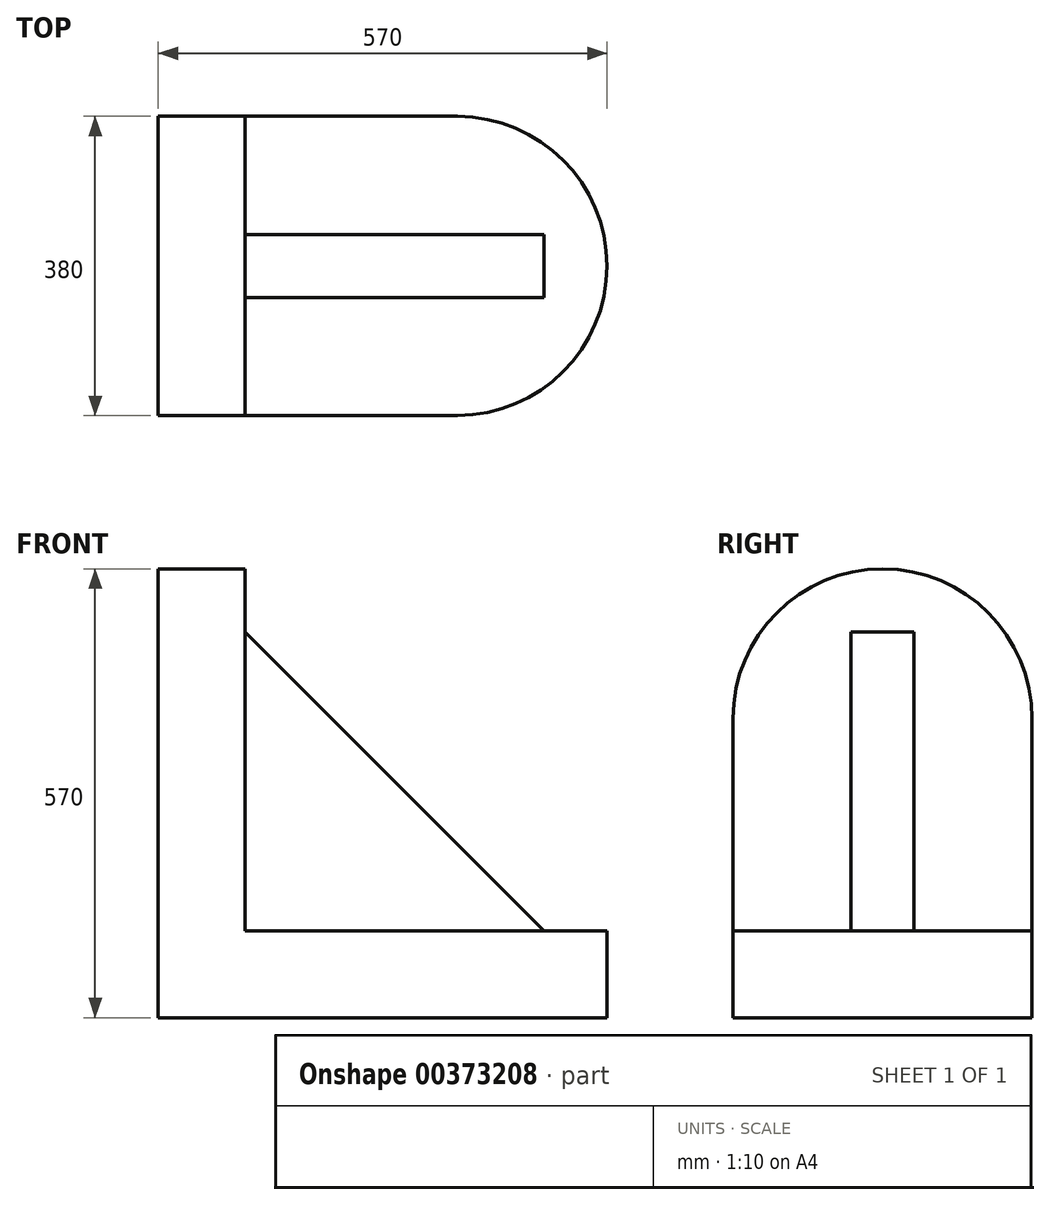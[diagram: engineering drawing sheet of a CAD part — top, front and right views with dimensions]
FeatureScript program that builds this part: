
annotation { "Feature Type Name" : "Feature", "Feature Type Description" : "" }
export const myFeature = defineFeature(function(context is Context, id is Id, definition is map)
    precondition{}
    {
        {
            var Q0;
            Q0=qCreatedBy(makeId("Top.planeOp"),FACE);
            var sketch = newSketch(context, id + "F0", { "sketchPlane" : qUnion([Q0])});
            skLineSegment(sketch, "E0.bottom", {"start": v(0, 0) * mm, "end": v(380, 0) * mm});
            skLineSegment(sketch, "E0.top", {"start": v(0, -380) * mm, "end": v(380, -380) * mm});
            skLineSegment(sketch, "E0.left", {"start": v(0, 0) * mm, "end": v(0, -380) * mm});
            skLineSegment(sketch, "E0.right", {"start": v(380, 0) * mm, "end": v(380, -380) * mm});
            skLineSegment(sketch, "E1", {"start": v(0, -380) * mm, "end": v(110, -380) * mm});
            skCircle(sketch, "E2", {"center": v(380, -190) * mm, "radius": 190 * mm});
            skSolve(sketch);
        }
        {
            var Q0;
            {var subQ1=sQuery(id+"F0.wireOp",EDGE,"E0.bottom");Q0=makeQuery(id+"F0.imprint","IMPRINT",FACE,{"disambiguationData":[TD([[makeQuery(id+"F0.imprint","IMPRINT",EDGE,{"derivedFrom":subQ1}),-1.0]])]});}
            var Q1;
            {var subQ0=sQuery(id+"F0.wireOp",EDGE,"E0.right");Q1=makeQuery(id+"F0.imprint","IMPRINT",FACE,{"disambiguationData":[TD([[makeQuery(id+"F0.imprint","IMPRINT",EDGE,{"derivedFrom":subQ0}),-1.0]])]});}
            var Q2;
            {var subQ0=sQuery(id+"F0.wireOp",EDGE,"E0.right");Q2=makeQuery(id+"F0.imprint","IMPRINT",FACE,{"disambiguationData":[TD([[makeQuery(id+"F0.imprint","IMPRINT",EDGE,{"derivedFrom":subQ0}),1.0]])]});}
            extrude(context, id + "F1", {"entities" : qUnion([Q0, Q1, Q2]), "depth" : 110 * mm});
        }
        {
            var Q0;
            Q0=makeQuery(id+"F1.opExtrude","CAP_FACE",FACE,{"disambiguationData":[OSD([sQuery(id+"F0.wireOp",EDGE,"E0.bottom"),sQuery(id+"F0.wireOp",EDGE,"E0.top"),sQuery(id+"F0.wireOp",EDGE,"E0.left"),sQuery(id+"F0.wireOp",EDGE,"E1"),sQuery(id+"F0.wireOp",EDGE,"E2")])],"isStart":false});
            var sketch = newSketch(context, id + "F2", { "sketchPlane" : qUnion([Q0])});
            skLineSegment(sketch, "E3.bottom", {"start": v(0, 0) * mm, "end": v(110, 0) * mm});
            skLineSegment(sketch, "E3.top", {"start": v(0, -380) * mm, "end": v(110, -380) * mm});
            skLineSegment(sketch, "E3.left", {"start": v(0, 0) * mm, "end": v(0, -380) * mm});
            skLineSegment(sketch, "E3.right", {"start": v(110, 0) * mm, "end": v(110, -380) * mm});
            skSolve(sketch);
        }
        {
            var Q0;
            Q0=makeQuery(id+"F2.imprint","IMPRINT",FACE,{"disambiguationData":[TD([[makeQuery(id+"F2.imprint","IMPRINT",EDGE,{"derivedFrom":sQuery(id+"F2.wireOp",EDGE,"E3.bottom")}),-1.0]])]});
            extrude(context, id + "F3", {"entities" : qUnion([Q0]), "operationType" : NewBodyOperationType.ADD, "depth" : 270 * mm});
        }
        {
            var Q0;
            Q0=makeQuery(id+"F3.boolean.opBoolean","MERGE",FACE,{"derivedFrom":[makeQuery(id+"F1.opExtrude","SWEPT_FACE",FACE,{"disambiguationData":[OSD([sQuery(id+"F0.wireOp",EDGE,"E0.left")])]}),makeQuery(id+"F3.opExtrude","SWEPT_FACE",FACE,{"disambiguationData":[OSD([sQuery(id+"F2.wireOp",EDGE,"E3.left")])]})]});
            var sketch = newSketch(context, id + "F4", { "sketchPlane" : qUnion([Q0])});
            skCircle(sketch, "E4", {"center": v(190, 380) * mm, "radius": 190 * mm});
            skSolve(sketch);
        }
        {
            var Q0;
            {var subQ1=sQuery(id+"F2.wireOp",EDGE,"E3.left");var subQ3=makeQuery(id+"F3.opExtrude","CAP_EDGE",EDGE,{"disambiguationData":[OSD([subQ1])],"isStart":false});Q0=makeQuery(id+"F4.imprint","IMPRINT",FACE,{"disambiguationData":[TD([[makeQuery(id+"F4.imprint","IMPRINT",EDGE,{"derivedFrom":subQ3}),1.0]])]});}
            extrude(context, id + "F5", {"entities" : qUnion([Q0]), "operationType" : NewBodyOperationType.ADD, "oppositeDirection" : true, "depth" : 110 * mm});
        }
        {
            var Q0;
            Q0=makeQuery(id+"F1.opExtrude","CAP_FACE",FACE,{"disambiguationData":[OSD([sQuery(id+"F0.wireOp",EDGE,"E0.bottom"),sQuery(id+"F0.wireOp",EDGE,"E0.top"),sQuery(id+"F0.wireOp",EDGE,"E0.left"),sQuery(id+"F0.wireOp",EDGE,"E1"),sQuery(id+"F0.wireOp",EDGE,"E2")])],"isStart":false});
            var sketch = newSketch(context, id + "F6", { "sketchPlane" : qUnion([Q0])});
            skLineSegment(sketch, "E5", {"start": v(110, -190) * mm, "end": v(490, -190) * mm});
            skLineSegment(sketch, "E6", {"start": v(490, -190) * mm, "end": v(490, -150) * mm});
            skLineSegment(sketch, "E7", {"start": v(490, -150) * mm, "end": v(110, -150) * mm});
            skLineSegment(sketch, "E8", {"start": v(110, -150) * mm, "end": v(110, -230) * mm});
            skLineSegment(sketch, "E9", {"start": v(490, -190) * mm, "end": v(490, -230) * mm});
            skLineSegment(sketch, "E10", {"start": v(490, -230) * mm, "end": v(110, -230) * mm});
            skSolve(sketch);
        }
        {
            var Q0;
            {var subQ0=sQuery(id+"F6.wireOp",EDGE,"E5");Q0=makeQuery(id+"F6.imprint","IMPRINT",FACE,{"disambiguationData":[TD([[makeQuery(id+"F6.imprint","IMPRINT",EDGE,{"derivedFrom":subQ0}),-1.0]])]});}
            var Q1;
            {var subQ0=sQuery(id+"F6.wireOp",EDGE,"E5");Q1=makeQuery(id+"F6.imprint","IMPRINT",FACE,{"disambiguationData":[TD([[makeQuery(id+"F6.imprint","IMPRINT",EDGE,{"derivedFrom":subQ0}),1.0]])]});}
            extrude(context, id + "F7", {"entities" : qUnion([Q0, Q1]), "operationType" : NewBodyOperationType.ADD, "depth" : 380 * mm});
        }
        {
            var Q0;
            Q0=makeQuery(id+"F7.opExtrude","SWEPT_FACE",FACE,{"disambiguationData":[OSD([sQuery(id+"F6.wireOp",EDGE,"E10")])]});
            var sketch = newSketch(context, id + "F8", { "sketchPlane" : qUnion([Q0])});
            skLineSegment(sketch, "E11", {"start": v(110, 490) * mm, "end": v(490, 110) * mm});
            skLineSegment(sketch, "E12", {"start": v(490, 110) * mm, "end": v(490, 490) * mm});
            skLineSegment(sketch, "E13", {"start": v(490, 490) * mm, "end": v(110, 490) * mm});
            skSolve(sketch);
        }
        {
            var Q0;
            Q0=makeQuery(id+"F8.imprint","IMPRINT",FACE,{"disambiguationData":[TD([[makeQuery(id+"F8.imprint","IMPRINT",EDGE,{"derivedFrom":sQuery(id+"F8.wireOp",EDGE,"E11")}),1.0]])]});
            extrude(context, id + "F9", {"entities" : qUnion([Q0]), "operationType" : NewBodyOperationType.REMOVE, "endBound" : BoundingType.THROUGH_ALL, "oppositeDirection" : true, "depth" : 25.4 * mm});
        }
    });
